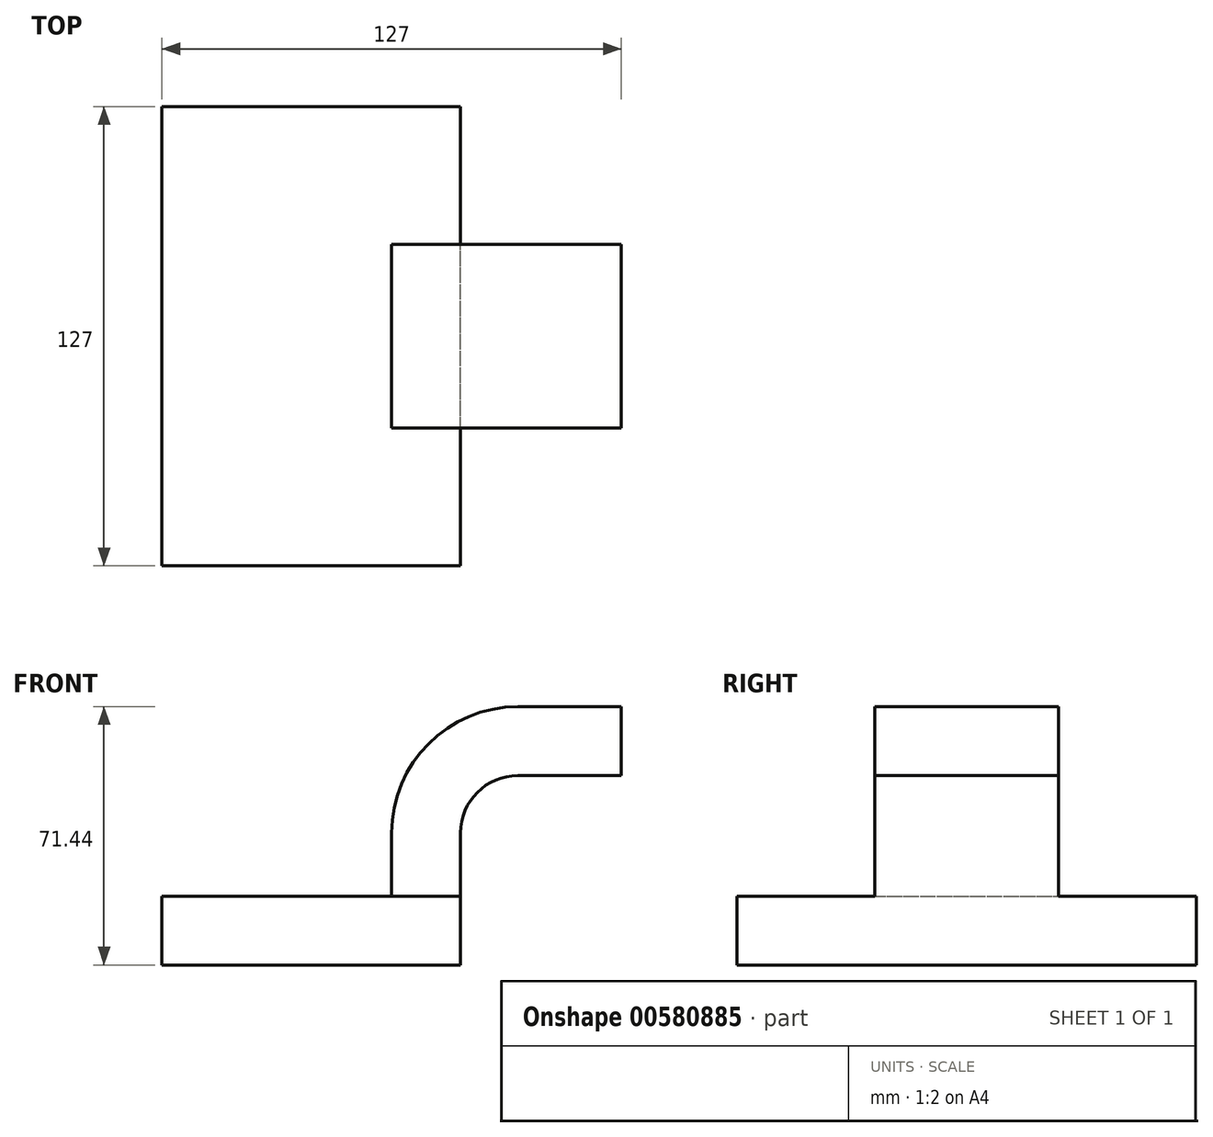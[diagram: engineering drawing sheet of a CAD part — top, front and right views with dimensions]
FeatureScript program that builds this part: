
annotation { "Feature Type Name" : "Feature", "Feature Type Description" : "" }
export const myFeature = defineFeature(function(context is Context, id is Id, definition is map)
    precondition{}
    {
        {
            var Q0;
            Q0=qCreatedBy(makeId("Front.planeOp"),FACE);
            var sketch = newSketch(context, id + "F0", { "sketchPlane" : qUnion([Q0])});
            skLineSegment(sketch, "E0.bottom", {"start": v(41.27, 9.53) * mm, "end": v(-41.28, 9.53) * mm});
            skLineSegment(sketch, "E0.top", {"start": v(41.28, -9.52) * mm, "end": v(-41.27, -9.52) * mm});
            skLineSegment(sketch, "E0.left", {"start": v(41.28, 9.53) * mm, "end": v(41.28, -9.52) * mm});
            skLineSegment(sketch, "E0.right", {"start": v(-41.28, 9.53) * mm, "end": v(-41.27, -9.52) * mm});
            skPoint(sketch, "E0.middle", {"position": v(0, 0) * mm});
            skLineSegment(sketch, "E1.bottom", {"start": v(111.13, 38.1) * mm, "end": v(60.32, 38.1) * mm});
            skLineSegment(sketch, "E1.top", {"start": v(111.13, 66.68) * mm, "end": v(60.33, 66.68) * mm});
            skLineSegment(sketch, "E1.left", {"start": v(111.13, 38.1) * mm, "end": v(111.13, 66.68) * mm});
            skLineSegment(sketch, "E1.right", {"start": v(60.33, 38.1) * mm, "end": v(60.33, 66.68) * mm});
            skPoint(sketch, "E1.middle", {"position": v(85.73, 52.39) * mm});
            skLineSegment(sketch, "E2", {"start": v(41.27, 9.53) * mm, "end": v(41.27, 26.99) * mm});
            skArc(sketch, "E3", {"start": v(41.27, 26.99) * mm, "mid": v(45.92, 38.21) * mm, "end": v(57.15, 42.86) * mm});
            skLineSegment(sketch, "E4", {"start": v(57.15, 42.86) * mm, "end": v(85.73, 42.86) * mm});
            skLineSegment(sketch, "E5.0", {"start": v(57.15, 61.91) * mm, "end": v(85.73, 61.91) * mm});
            skArc(sketch, "E5.1", {"start": v(22.23, 26.99) * mm, "mid": v(32.45, 51.68) * mm, "end": v(57.15, 61.91) * mm});
            skLineSegment(sketch, "E5.2", {"start": v(22.23, 9.53) * mm, "end": v(22.23, 26.99) * mm});
            skLineSegment(sketch, "E6", {"start": v(85.73, 61.91) * mm, "end": v(85.73, 42.86) * mm});
            skFitSpline(sketch, "E7", {"points": [v(-41.27, 9.53) * mm, v(57.15, 61.91) * mm], "startDerivative": vector(0, 81.96) * mm, "endDerivative": vector(139.78, 0) * mm});
            skLineSegment(sketch, "E8", {"start": v(85.73, 38.1) * mm, "end": v(85.73, 66.68) * mm, "construction": true});
            skSolve(sketch);
        }
        {
            var Q0;
            Q0=makeQuery(id+"F0.imprint","IMPRINT",FACE,{"disambiguationData":[TD([[makeQuery(id+"F0.imprint","IMPRINT",EDGE,{"derivedFrom":sQuery(id+"F0.wireOp",EDGE,"E0.top")}),-1.0]])]});
            extrude(context, id + "F1", {"entities" : qUnion([Q0]), "endBound" : BoundingType.SYMMETRIC, "depth" : 127 * mm, "offsetDistance" : 25.4 * mm});
        }
        {
            var Q0;
            {var subQ1=sQuery(id+"F0.wireOp",EDGE,"E2");Q0=makeQuery(id+"F0.imprint","IMPRINT",FACE,{"disambiguationData":[TD([[makeQuery(id+"F0.imprint","IMPRINT",EDGE,{"derivedFrom":subQ1}),1.0]])]});}
            var Q1;
            {var subQ0=sQuery(id+"F0.wireOp",EDGE,"E4");var subQ1=sQuery(id+"F0.wireOp",EDGE,"E1.right");var subQ2=makeQuery(id+"F0.imprint","INTERSECT",VERTEX,{"derivedFrom":[subQ1,subQ0]});Q1=makeQuery(id+"F0.imprint","IMPRINT",FACE,{"disambiguationData":[TD([[makeQuery(id+"F0.imprint","IMPRINT",EDGE,{"disambiguationData":[TD([[subQ2,-1.0]])],"derivedFrom":subQ1}),-1.0]])]});}
            extrude(context, id + "F2", {"entities" : qUnion([Q0, Q1]), "operationType" : NewBodyOperationType.ADD, "endBound" : BoundingType.SYMMETRIC, "depth" : 50.8 * mm, "offsetDistance" : 25.4 * mm});
        }
        {
            var Q0;
            Q0=makeQuery(id+"F0.imprint","IMPRINT",FACE,{"disambiguationData":[TD([[makeQuery(id+"F0.imprint","IMPRINT",EDGE,{"derivedFrom":sQuery(id+"F0.wireOp",EDGE,"E5.1")}),1.0]])]});
            extrude(context, id + "F3", {"entities" : qUnion([Q0]), "operationType" : NewBodyOperationType.ADD, "endBound" : BoundingType.SYMMETRIC, "depth" : 25.4 * mm, "offsetDistance" : 25.4 * mm});
        }
    });
